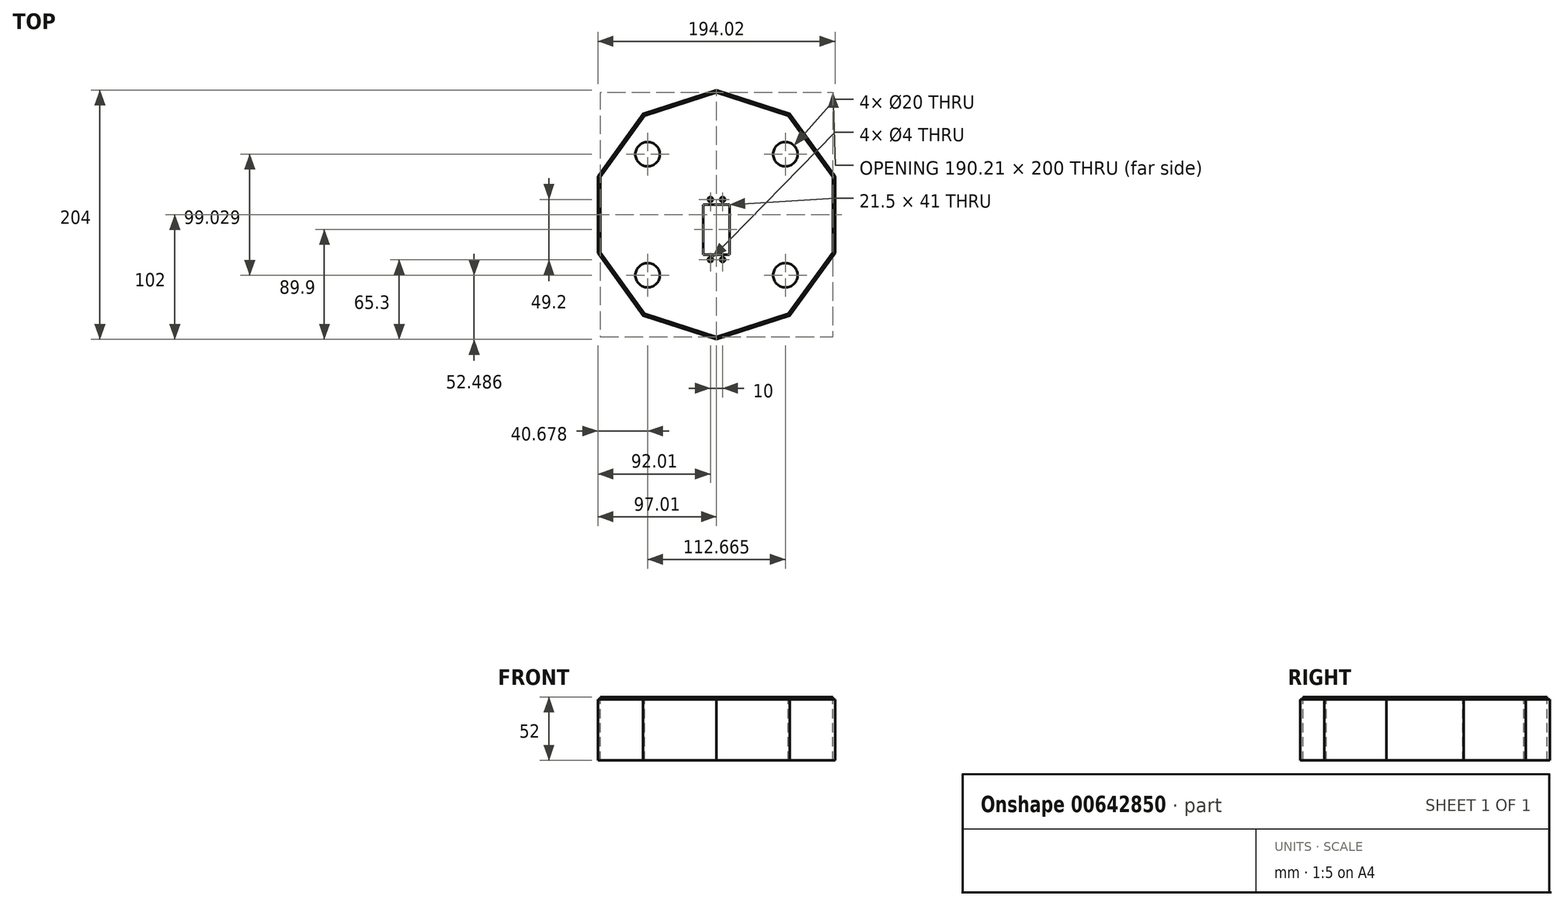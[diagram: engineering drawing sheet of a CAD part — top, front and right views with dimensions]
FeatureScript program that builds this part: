
annotation { "Feature Type Name" : "Feature", "Feature Type Description" : "" }
export const myFeature = defineFeature(function(context is Context, id is Id, definition is map)
    precondition{}
    {
        {
            var Q0;
            Q0=qCreatedBy(makeId("Top.planeOp"),FACE);
            var sketch = newSketch(context, id + "F0", { "sketchPlane" : qUnion([Q0])});
            skCircle(sketch, "E0.cCircle", {"center": v(0, 0) * mm, "radius": 100 * mm, "construction": true});
            skLineSegment(sketch, "E0.0", {"start": v(0, 100) * mm, "end": v(58.78, 80.9) * mm});
            skLineSegment(sketch, "E0.1", {"start": v(58.78, 80.9) * mm, "end": v(95.1, 30.9) * mm});
            skLineSegment(sketch, "E0.2", {"start": v(95.1, 30.9) * mm, "end": v(95.1, -30.9) * mm});
            skLineSegment(sketch, "E0.3", {"start": v(95.1, -30.9) * mm, "end": v(58.78, -80.9) * mm});
            skLineSegment(sketch, "E0.4", {"start": v(58.78, -80.9) * mm, "end": v(0, -100) * mm});
            skLineSegment(sketch, "E0.5", {"start": v(0, -100) * mm, "end": v(-58.78, -80.9) * mm});
            skLineSegment(sketch, "E0.6", {"start": v(-58.78, -80.9) * mm, "end": v(-95.1, -30.9) * mm});
            skLineSegment(sketch, "E0.7", {"start": v(-95.1, -30.9) * mm, "end": v(-95.1, 30.9) * mm});
            skLineSegment(sketch, "E0.8", {"start": v(-95.1, 30.9) * mm, "end": v(-58.78, 80.9) * mm});
            skLineSegment(sketch, "E0.9", {"start": v(-58.78, 80.9) * mm, "end": v(0, 100) * mm});
            skLineSegment(sketch, "E1.bottom", {"start": v(-10.75, 8.4) * mm, "end": v(10.75, 8.4) * mm});
            skLineSegment(sketch, "E1.top", {"start": v(-10.75, -32.6) * mm, "end": v(10.75, -32.6) * mm});
            skLineSegment(sketch, "E1.left", {"start": v(-10.75, 8.4) * mm, "end": v(-10.75, -32.6) * mm});
            skLineSegment(sketch, "E1.right", {"start": v(10.75, 8.4) * mm, "end": v(10.75, -32.6) * mm});
            skCircle(sketch, "E2", {"center": v(-5, 12.5) * mm, "radius": 2 * mm});
            skCircle(sketch, "E3", {"center": v(5, 12.5) * mm, "radius": 2 * mm});
            skCircle(sketch, "E4", {"center": v(-5, -36.7) * mm, "radius": 2 * mm});
            skCircle(sketch, "E5", {"center": v(5, -36.7) * mm, "radius": 2 * mm});
            skCircle(sketch, "E6", {"center": v(-56.33, 49.51) * mm, "radius": 10 * mm});
            skCircle(sketch, "E7", {"center": v(56.33, 49.51) * mm, "radius": 10 * mm});
            skCircle(sketch, "E8", {"center": v(-56.33, -49.51) * mm, "radius": 10 * mm});
            skCircle(sketch, "E9", {"center": v(56.33, -49.51) * mm, "radius": 10 * mm});
            skCircle(sketch, "E10.cCircle", {"center": v(0, 0) * mm, "radius": 102 * mm, "construction": true});
            skLineSegment(sketch, "E10.0", {"start": v(0, 102) * mm, "end": v(59.95, 82.52) * mm});
            skLineSegment(sketch, "E10.1", {"start": v(59.95, 82.52) * mm, "end": v(97, 31.52) * mm});
            skLineSegment(sketch, "E10.2", {"start": v(97, 31.52) * mm, "end": v(97, -31.52) * mm});
            skLineSegment(sketch, "E10.3", {"start": v(97, -31.52) * mm, "end": v(59.95, -82.52) * mm});
            skLineSegment(sketch, "E10.4", {"start": v(59.95, -82.52) * mm, "end": v(0, -102) * mm});
            skLineSegment(sketch, "E10.5", {"start": v(0, -102) * mm, "end": v(-59.95, -82.52) * mm});
            skLineSegment(sketch, "E10.6", {"start": v(-59.95, -82.52) * mm, "end": v(-97, -31.52) * mm});
            skLineSegment(sketch, "E10.7", {"start": v(-97, -31.52) * mm, "end": v(-97, 31.52) * mm});
            skLineSegment(sketch, "E10.8", {"start": v(-97, 31.52) * mm, "end": v(-59.95, 82.52) * mm});
            skLineSegment(sketch, "E10.9", {"start": v(-59.95, 82.52) * mm, "end": v(0, 102) * mm});
            skSolve(sketch);
        }
        {
            var Q0;
            Q0=makeQuery(id+"F0.imprint","IMPRINT",FACE,{"disambiguationData":[TD([[makeQuery(id+"F0.imprint","IMPRINT",EDGE,{"derivedFrom":sQuery(id+"F0.wireOp",EDGE,"E0.0")}),-1.0]])]});
            extrude(context, id + "F1", {"entities" : qUnion([Q0]), "depth" : 2 * mm, "offsetDistance" : 25 * mm});
        }
        {
            var Q0;
            Q0=qSketchRegion(id+"F0",true);
            extrude(context, id + "F2", {"entities" : qUnion([Q0]), "depth" : -50 * mm, "offsetDistance" : 25 * mm});
        }
    });
